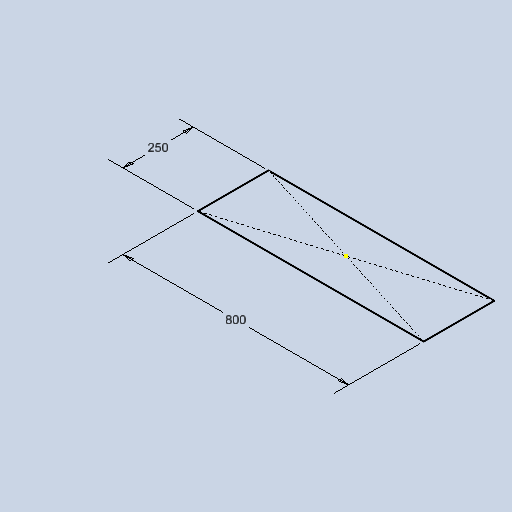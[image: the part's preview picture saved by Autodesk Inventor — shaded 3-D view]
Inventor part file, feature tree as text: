
AUTODESK INVENTOR PART (.ipt)
format: ipt  version: 2025 (Build 290162010, 162A)  size: 76,288 bytes
history: native  units: mm
features: sketch x1
ambient origin geometry x8: Origin, YZ Plane, XZ Plane, XY Plane, X Axis, Y Axis, Z Axis, Center Point
feature tree (1):
  sketch  "Sketch1"  dims[d0=800.0mm d1=250.0mm]
